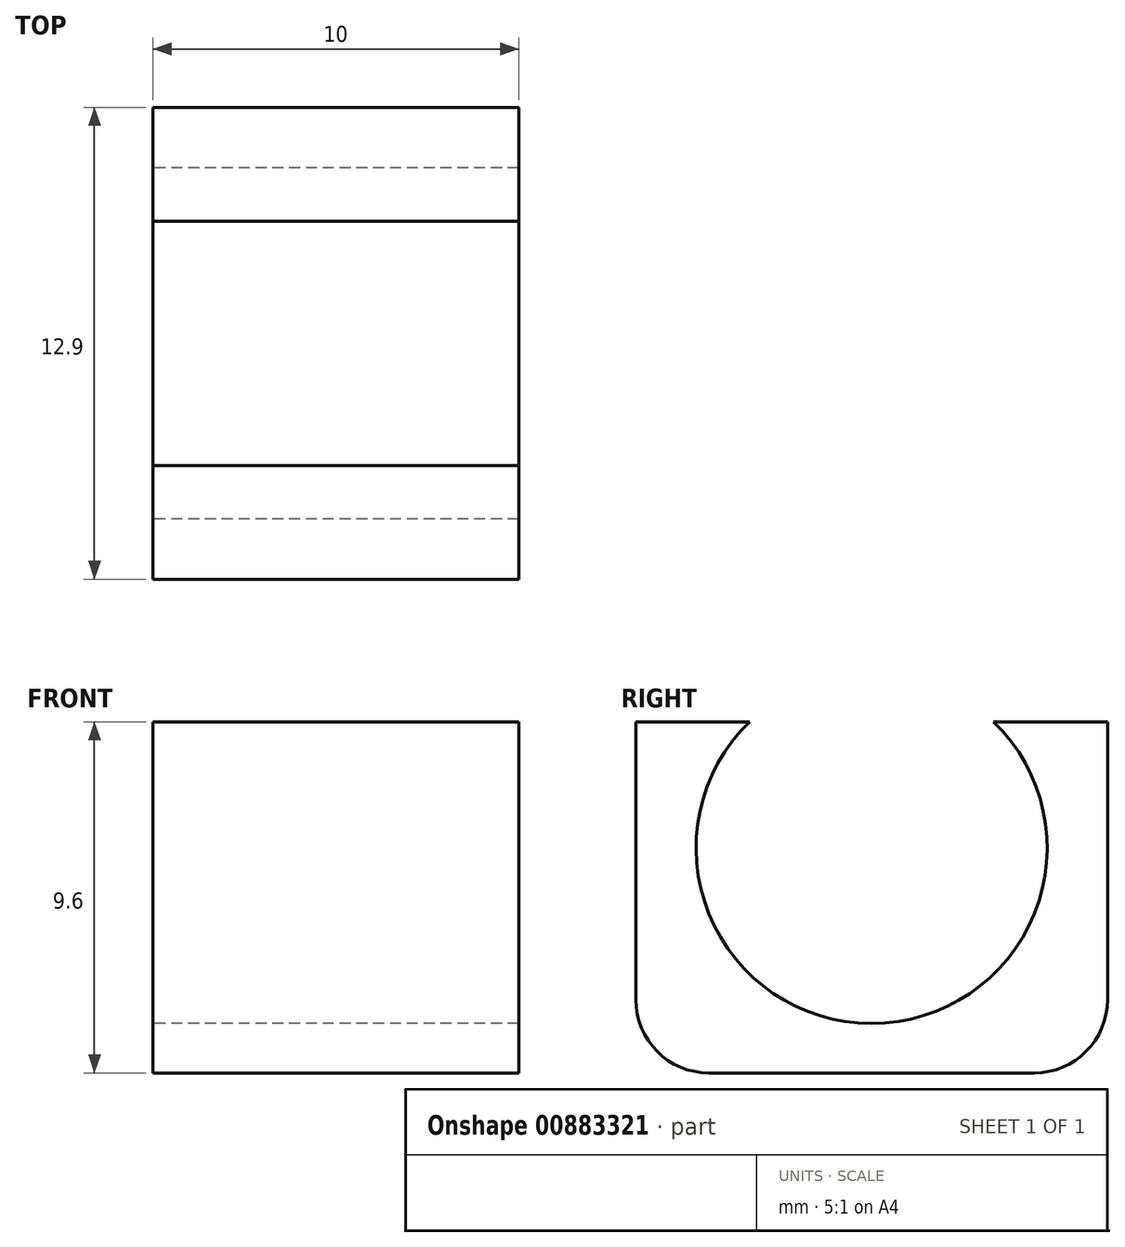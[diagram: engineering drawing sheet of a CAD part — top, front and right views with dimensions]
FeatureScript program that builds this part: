
annotation { "Feature Type Name" : "Feature", "Feature Type Description" : "" }
export const myFeature = defineFeature(function(context is Context, id is Id, definition is map)
    precondition{}
    {
        {
            var Q0;
            Q0=qCreatedBy(makeId("Top.planeOp"),FACE);
            var sketch = newSketch(context, id + "F0", { "sketchPlane" : qUnion([Q0])});
            skLineSegment(sketch, "E0.bottom", {"start": v(5, -6.45) * mm, "end": v(-5, -6.45) * mm});
            skLineSegment(sketch, "E0.top", {"start": v(5, 6.45) * mm, "end": v(-5, 6.45) * mm});
            skLineSegment(sketch, "E0.left", {"start": v(5, -6.45) * mm, "end": v(5, 6.45) * mm});
            skLineSegment(sketch, "E0.right", {"start": v(-5, -6.45) * mm, "end": v(-5, 6.45) * mm});
            skPoint(sketch, "E0.middle", {"position": v(0, 0) * mm});
            skSolve(sketch);
        }
        {
            var Q0;
            Q0=makeQuery(id+"F0.imprint","IMPRINT",FACE,{"disambiguationData":[TD([[makeQuery(id+"F0.imprint","IMPRINT",EDGE,{"derivedFrom":sQuery(id+"F0.wireOp",EDGE,"E0.bottom")}),-1.0]])]});
            extrude(context, id + "F1", {"entities" : qUnion([Q0]), "depth" : 9.6 * mm, "offsetDistance" : 25 * mm});
        }
        {
            var Q0;
            Q0=makeQuery(id+"F1.opExtrude","SWEPT_FACE",FACE,{"disambiguationData":[OSD([sQuery(id+"F0.wireOp",EDGE,"E0.right")])]});
            var sketch = newSketch(context, id + "F2", { "sketchPlane" : qUnion([Q0])});
            skLineSegment(sketch, "E1", {"start": v(0, 0) * mm, "end": v(0, 6.15) * mm});
            skCircle(sketch, "E2", {"center": v(0, 6.15) * mm, "radius": 4.8 * mm});
            skLineSegment(sketch, "E3", {"start": v(0, 6.15) * mm, "end": v(4.8, 6.15) * mm});
            skLineSegment(sketch, "E4", {"start": v(0, 6.15) * mm, "end": v(-4.8, 6.15) * mm});
            skSolve(sketch);
        }
        {
            var Q0;
            {var subQ5=sQuery(id+"F2.wireOp",EDGE,"E3");Q0=makeQuery(id+"F2.imprint","IMPRINT",FACE,{"disambiguationData":[TD([[makeQuery(id+"F2.imprint","IMPRINT",EDGE,{"derivedFrom":subQ5}),1.0]])]});}
            var Q1;
            {var subQ0=sQuery(id+"F2.wireOp",EDGE,"E4");Q1=makeQuery(id+"F2.imprint","IMPRINT",FACE,{"disambiguationData":[TD([[makeQuery(id+"F2.imprint","IMPRINT",EDGE,{"derivedFrom":subQ0}),1.0]])]});}
            var Q2;
            {var subQ0=sQuery(id+"F2.wireOp",EDGE,"E3");Q2=makeQuery(id+"F2.imprint","IMPRINT",FACE,{"disambiguationData":[TD([[makeQuery(id+"F2.imprint","IMPRINT",EDGE,{"derivedFrom":subQ0}),-1.0]])]});}
            extrude(context, id + "F3", {"entities" : qUnion([Q0, Q1, Q2]), "operationType" : NewBodyOperationType.REMOVE, "endBound" : BoundingType.THROUGH_ALL, "oppositeDirection" : true, "depth" : 25 * mm, "offsetDistance" : 25 * mm});
        }
        {
            var Q0;
            Q0=makeQuery(id+"F1.opExtrude","CAP_EDGE",EDGE,{"disambiguationData":[OSD([sQuery(id+"F0.wireOp",EDGE,"E0.bottom")])],"isStart":true});
            var Q1;
            Q1=makeQuery(id+"F1.opExtrude","CAP_EDGE",EDGE,{"disambiguationData":[OSD([sQuery(id+"F0.wireOp",EDGE,"E0.top")])],"isStart":true});
            fillet(context, id + "F4", {"entities" : qUnion([Q0, Q1]), "radius" : 2 * mm, "tangentPropagation" : true, "allowEdgeOverflow" : false});
        }
    });
